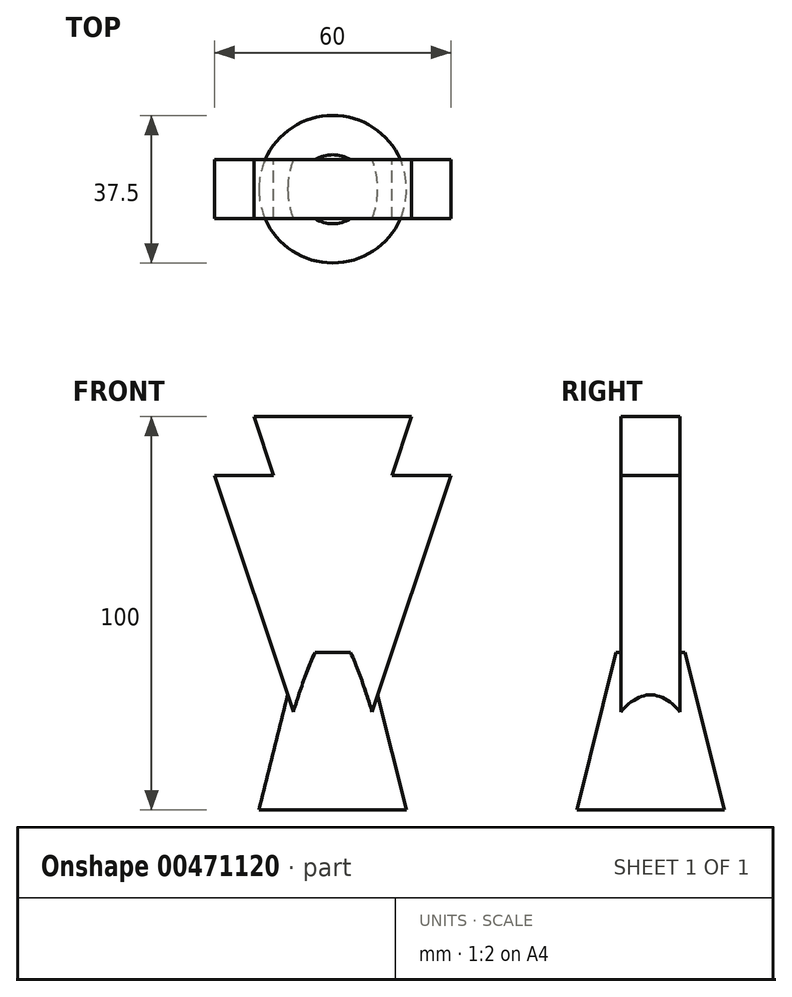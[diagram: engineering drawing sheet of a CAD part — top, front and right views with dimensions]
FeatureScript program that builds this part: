
annotation { "Feature Type Name" : "Feature", "Feature Type Description" : "" }
export const myFeature = defineFeature(function(context is Context, id is Id, definition is map)
    precondition{}
    {
        {
            var Q0;
            Q0=qCreatedBy(makeId("Front.planeOp"),FACE);
            var sketch = newSketch(context, id + "F0", { "sketchPlane" : qUnion([Q0])});
            skLineSegment(sketch, "E0.top", {"start": v(-35, 40.57) * mm, "end": v(5, 40.57) * mm});
            skLineSegment(sketch, "E1", {"start": v(-15, 40.57) * mm, "end": v(-15, 25.57) * mm});
            skLineSegment(sketch, "E2", {"start": v(-15, 25.57) * mm, "end": v(-30, 25.57) * mm});
            skLineSegment(sketch, "E3", {"start": v(-15, 25.57) * mm, "end": v(0, 25.57) * mm});
            skLineSegment(sketch, "E4", {"start": v(-35, 40.57) * mm, "end": v(-30, 25.57) * mm});
            skLineSegment(sketch, "E5", {"start": v(0, 25.57) * mm, "end": v(5, 40.57) * mm});
            skLineSegment(sketch, "E6", {"start": v(-30, 25.57) * mm, "end": v(-45, 25.57) * mm});
            skLineSegment(sketch, "E7", {"start": v(-45, 25.57) * mm, "end": v(-30, -19.43) * mm});
            skLineSegment(sketch, "E8", {"start": v(-30, -19.43) * mm, "end": v(0, -19.43) * mm});
            skLineSegment(sketch, "E9", {"start": v(0, -19.43) * mm, "end": v(15, 25.57) * mm});
            skLineSegment(sketch, "E10", {"start": v(15, 25.57) * mm, "end": v(0, 25.57) * mm});
            skSolve(sketch);
        }
        {
            var Q0;
            {var subQ2=sQuery(id+"F0.wireOp",EDGE,"E1");Q0=makeQuery(id+"F0.imprint","IMPRINT",FACE,{"disambiguationData":[TD([[makeQuery(id+"F0.imprint","IMPRINT",EDGE,{"derivedFrom":subQ2}),-1.0]])]});}
            var Q1;
            {var subQ2=sQuery(id+"F0.wireOp",EDGE,"E1");Q1=makeQuery(id+"F0.imprint","IMPRINT",FACE,{"disambiguationData":[TD([[makeQuery(id+"F0.imprint","IMPRINT",EDGE,{"derivedFrom":subQ2}),1.0]])]});}
            var Q2;
            Q2=makeQuery(id+"F0.imprint","IMPRINT",FACE,{"disambiguationData":[TD([[makeQuery(id+"F0.imprint","IMPRINT",EDGE,{"derivedFrom":sQuery(id+"F0.wireOp",EDGE,"E2")}),1.0]])]});
            extrude(context, id + "F1", {"entities" : qUnion([Q0, Q1, Q2]), "depth" : 15 * mm});
        }
        {
            var Q0;
            Q0=makeQuery(id+"F1.opExtrude","SWEPT_FACE",FACE,{"disambiguationData":[OSD([sQuery(id+"F0.wireOp",EDGE,"E8")])]});
            var sketch = newSketch(context, id + "F2", { "sketchPlane" : qUnion([Q0])});
            skCircle(sketch, "E11", {"center": v(-15, 7.5) * mm, "radius": 18.75 * mm});
            skPoint(sketch, "E11.centerSnap0", {"position": v(-15, 15) * mm});
            skSolve(sketch);
        }
        {
            var Q0;
            Q0 = qSketchRegion(id + "F2", true);
            extrude(context, id + "F3", {"entities" : qUnion([Q0]), "operationType" : NewBodyOperationType.ADD, "depth" : 40 * mm});
        }
        {
            var Q0;
            Q0=makeQuery(id+"F3.opExtrude","CAP_EDGE",EDGE,{"disambiguationData":[OSD([sQuery(id+"F2.wireOp",EDGE,"E11")])],"isStart":true});
            chamfer(context, id + "F4", {"entities" : qUnion([Q0]), "chamferType" : ChamferType.TWO_OFFSETS, "width1" : 10 * mm, "oppositeDirection" : true, "width2" : 40 * mm, "tangentPropagation" : true});
        }
    });
